# Revit family: 820-10-028-DN80-150
name_source: partatom
category: Pipe Accessories
units: mm (PartAtom-declared; Revit-internal decimal feet)

## family parameters
Always vertical = Yes
Cut with Voids When Loaded = No
Part Type = Valve - Breaks Into
Round Connector Dimension = Use Diameter
Shared = No
Work Plane-Based = No

## types (4) — shared parameters
2 = 2 mm  [stored 0.00656168 ft]
Body_wallthickness = 10 mm  [stored 0.0328084 ft]
DN080_PN10/16 = 820-0080-10-521L0160002
DN100_PN10/16 = 820-0100-10-521L0160002
DN125_PN10/16 = 820-0125-10-521L0160002
DN150_PN10/16 = 820-0150-10-521L0160002
Description_ = AVK CENTRIC BUTTERFLY VALVE LUG TYPE, PN10/16
Flange_thickness = 10 mm  [stored 0.0328084 ft]
Search_table = 820-10-028-DN80-150
URL product pages = https://www.avkvalves.com 820008010521L0160002
fillet = 20 mm  [stored 0.0656168 ft]
zero-valued in all types: Default Elevation

## per-type parameters (varying)
| type | Actuator_Dia | DN | EPDM | F | F2 | H2 | Hole_dia | Hole_l | ID | L | L2 | LUG_T | L_ref | L_ref_2 | L_ref_3 | Lug_D | Lug_D1 | PCD | Rubber_R | W2_ref | disk |
| DN080_PN10/16 | 65 mm  [stored 0.213255 ft] | 80 mm | 39 mm  [stored 0.127953 ft] | 11 mm  [stored 0.0360892 ft] | 12 mm  [stored 0.0393701 ft] | 88 mm | 19 mm  [stored 0.062336 ft] | 82 mm | 40 mm  [stored 0.131234 ft] | 46 mm  [stored 0.150919 ft] | 94 mm | 18 mm | 26 mm | 52 mm | 22 mm | 12 mm  [stored 0.0393701 ft] | 21 mm | 80 mm | 45 mm  [stored 0.147638 ft] | 160 mm | 13 mm  [stored 0.0426509 ft] |
| DN150_PN10/16 | 90 mm | 150 mm | 74 mm  [stored 0.242782 ft] | 14 mm  [stored 0.0459318 ft] | 16 mm  [stored 0.0524934 ft] | 128 mm | 28 mm  [stored 0.0918635 ft] | 120 mm | 75 mm | 56 mm  [stored 0.183727 ft] | 137 mm | 22 mm | 36 mm  [stored 0.11811 ft] | 72 mm  [stored 0.23622 ft] | 30 mm  [stored 0.0984252 ft] | 18 mm | 31 mm  [stored 0.101706 ft] | 125 mm | 80 mm | 210 mm | 16 mm  [stored 0.0524934 ft] |
| DN125_PN10/16 | 90 mm | 125 mm | 62 mm  [stored 0.203412 ft] | 14 mm  [stored 0.0459318 ft] | 16 mm  [stored 0.0524934 ft] | 116 mm | 28 mm  [stored 0.0918635 ft] | 107 mm | 63 mm  [stored 0.206693 ft] | 56 mm  [stored 0.183727 ft] | 124 mm | 22 mm | 36 mm  [stored 0.11811 ft] | 72 mm  [stored 0.23622 ft] | 30 mm  [stored 0.0984252 ft] | 18 mm | 31 mm  [stored 0.101706 ft] | 110 mm | 68 mm  [stored 0.223097 ft] | 195 mm | 16 mm  [stored 0.0524934 ft] |
| DN100_PN10/16 | 90 mm | 100 mm | 49 mm  [stored 0.160761 ft] | 11 mm  [stored 0.0360892 ft] | 12 mm  [stored 0.0393701 ft] | 102 mm | 23 mm  [stored 0.0754593 ft] | 95 mm | 50 mm  [stored 0.164042 ft] | 52 mm | 110 mm | 21 mm | 32 mm  [stored 0.104987 ft] | 64 mm  [stored 0.209974 ft] | 27 mm | 14 mm  [stored 0.0459318 ft] | 25 mm  [stored 0.082021 ft] | 95 mm | 55 mm  [stored 0.180446 ft] | 180 mm | 15 mm  [stored 0.0492126 ft] |

note: [stored X ft] marks values corroborated as IEEE doubles in the binary element streams (Revit-internal decimal feet)

## geometry (parser evidence)
native form markers: Sweep x4
no freeform markers — native parametric forms only
